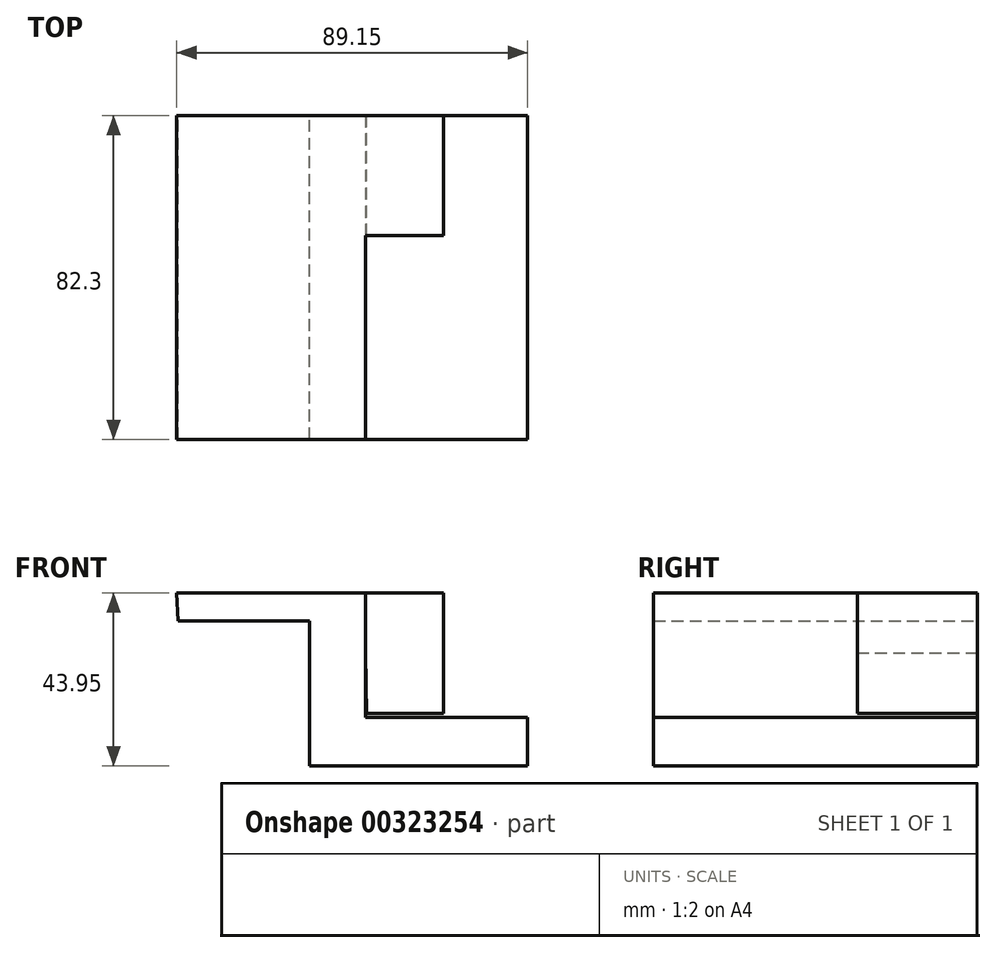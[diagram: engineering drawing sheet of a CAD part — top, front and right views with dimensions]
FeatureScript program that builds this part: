
annotation { "Feature Type Name" : "Feature", "Feature Type Description" : "" }
export const myFeature = defineFeature(function(context is Context, id is Id, definition is map)
    precondition{}
    {
        {
            var Q0;
            Q0=qCreatedBy(makeId("Front.planeOp"),FACE);
            var sketch = newSketch(context, id + "F0", { "sketchPlane" : qUnion([Q0])});
            skLineSegment(sketch, "E0", {"start": v(-54.17, 41.32) * mm, "end": v(-19.5, 41.32) * mm});
            skLineSegment(sketch, "E1", {"start": v(-53.86, 34.2) * mm, "end": v(-20.43, 34.2) * mm});
            skLineSegment(sketch, "E2", {"start": v(-20.43, 34.2) * mm, "end": v(-20.43, 18.1) * mm});
            skLineSegment(sketch, "E3", {"start": v(-20.43, 18.1) * mm, "end": v(-20.43, -2.63) * mm});
            skLineSegment(sketch, "E4", {"start": v(-20.43, -2.63) * mm, "end": v(34.98, -2.63) * mm});
            skLineSegment(sketch, "E5", {"start": v(34.98, -2.63) * mm, "end": v(34.98, 9.75) * mm});
            skLineSegment(sketch, "E6", {"start": v(34.98, 9.75) * mm, "end": v(-6.2, 9.75) * mm});
            skLineSegment(sketch, "E7", {"start": v(-6.2, 9.75) * mm, "end": v(-6.2, 41.32) * mm});
            skLineSegment(sketch, "E8", {"start": v(-6.2, 41.32) * mm, "end": v(-19.5, 41.32) * mm});
            skLineSegment(sketch, "E9", {"start": v(-54.17, 41.32) * mm, "end": v(-53.86, 34.2) * mm});
            skSolve(sketch);
        }
        {
            var Q0;
            Q0=makeQuery(id+"F0.imprint","IMPRINT",FACE,{"disambiguationData":[TD([[makeQuery(id+"F0.imprint","IMPRINT",EDGE,{"derivedFrom":sQuery(id+"F0.wireOp",EDGE,"E0")}),-1.0]])]});
            extrude(context, id + "F1", {"entities" : qUnion([Q0]), "depth" : 82.3 * mm});
        }
        {
            var Q0;
            Q0=qCreatedBy(makeId("Front.planeOp"),FACE);
            var sketch = newSketch(context, id + "F2", { "sketchPlane" : qUnion([Q0])});
            skLineSegment(sketch, "E10", {"start": v(-6.5, 41.32) * mm, "end": v(13.62, 41.32) * mm});
            skLineSegment(sketch, "E11", {"start": v(13.62, 41.32) * mm, "end": v(13.62, 10.68) * mm});
            skLineSegment(sketch, "E12", {"start": v(13.62, 10.68) * mm, "end": v(-5.88, 10.68) * mm});
            skLineSegment(sketch, "E13", {"start": v(-5.88, 10.68) * mm, "end": v(-6.5, 41.32) * mm});
            skSolve(sketch);
        }
        {
            var Q0;
            Q0=makeQuery(id+"F2.imprint","IMPRINT",FACE,{"disambiguationData":[TD([[makeQuery(id+"F2.imprint","IMPRINT",EDGE,{"derivedFrom":sQuery(id+"F2.wireOp",EDGE,"E10")}),-1.0]])]});
            extrude(context, id + "F3", {"entities" : qUnion([Q0]), "operationType" : NewBodyOperationType.ADD, "depth" : 17.02 * mm});
        }
        {
            var Q0;
            Q0=makeQuery(id+"F3.opExtrude","CAP_FACE",FACE,{"disambiguationData":[OSD([sQuery(id+"F2.wireOp",EDGE,"E10"),sQuery(id+"F2.wireOp",EDGE,"E11"),sQuery(id+"F2.wireOp",EDGE,"E12"),sQuery(id+"F2.wireOp",EDGE,"E13")])],"isStart":false});
            extrude(context, id + "F4", {"entities" : qUnion([Q0]), "operationType" : NewBodyOperationType.ADD, "depth" : 13.46 * mm});
        }
    });
